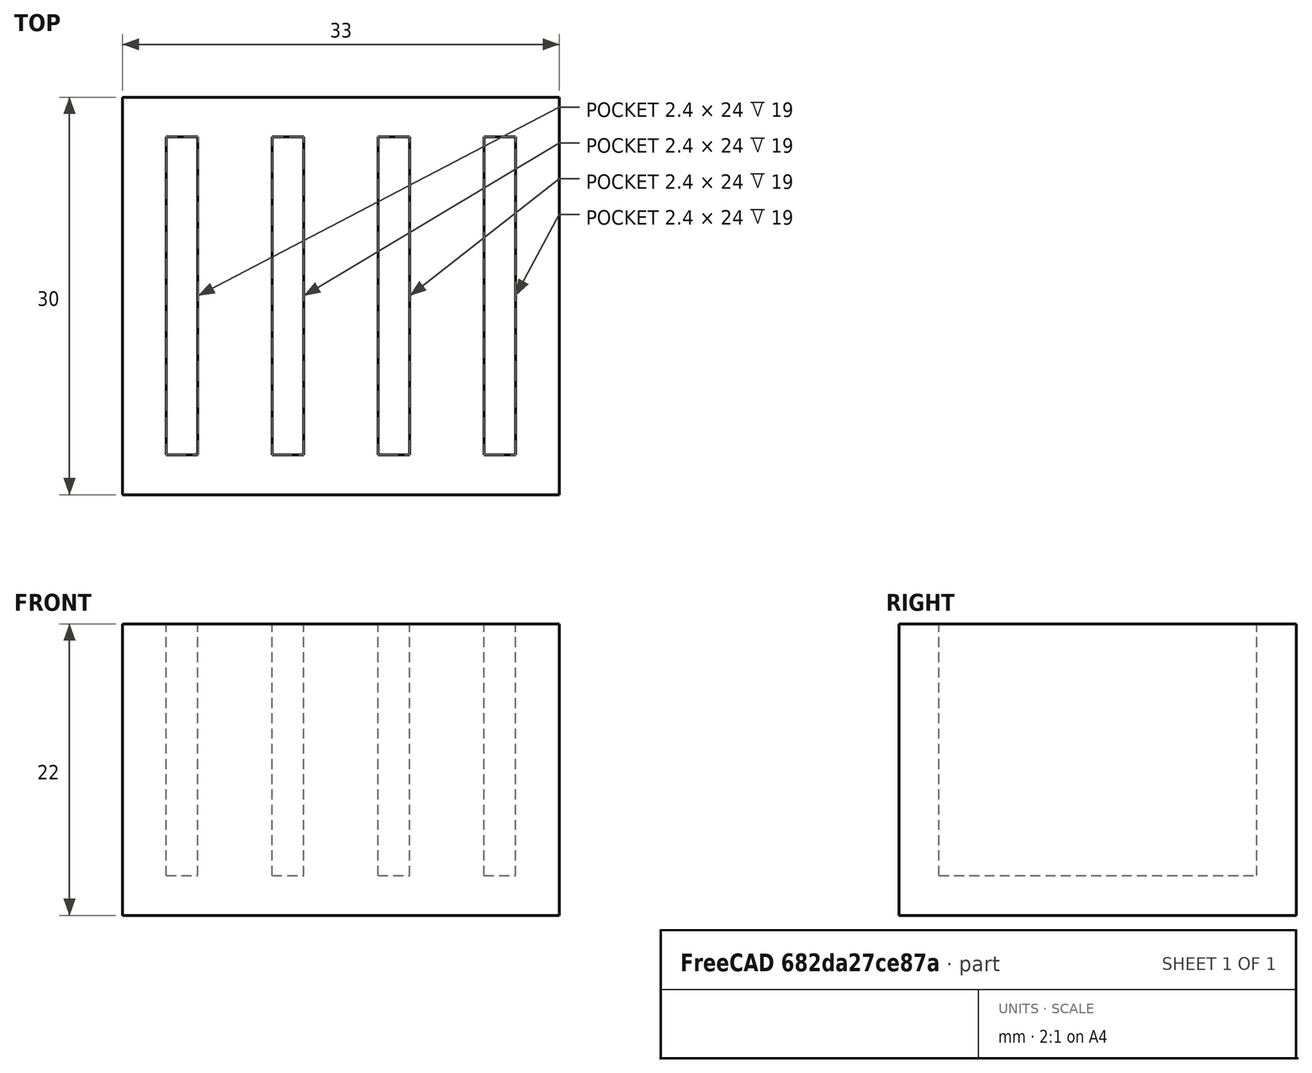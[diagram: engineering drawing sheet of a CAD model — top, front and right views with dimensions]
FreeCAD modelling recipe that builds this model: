
FCSTD DOCUMENT  (FreeCAD 1.0R39319 (Git))
Label: ojt1_t08r01_sd_holder
License: All rights reserved
LicenseURL: https://en.wikipedia.org/wiki/All_rights_reserved
objects: Part::Box×5, PartDesign::Body×1, Part::MultiFuse×1, Part::Cut×1
note: 8 computed .brp shape members not serialized (recipe doc carries the construction recipe); baked Part::Feature solids carry a one-line shape summary decoded from their .brp

FEATURE [PartDesign::Body] Body  label="Cos"
  AllowCompound = false
  Origin = -> Origin
FEATURE [Part::Box] Box004  label="base"
  AttacherType = Attacher::AttachEngine3D
  Height = 22
  Length = 33
  Width = 30
FEATURE [Part::Box] Box  label="cub 1"
  AttacherType = Attacher::AttachEngine3D
  Height = 30
  Length = 2.4
  Placement = pos=(3.3,3,0) rot=(0,0,1;0rad)
  Width = 24
FEATURE [Part::Box] Box007  label="cub 2"
  AttacherType = Attacher::AttachEngine3D
  Height = 30
  Length = 2.4
  Placement = pos=(11.3,3,0) rot=(0,0,1;0rad)
  Width = 24
FEATURE [Part::Box] Box008  label="cub 3"
  AttacherType = Attacher::AttachEngine3D
  Height = 30
  Length = 2.4
  Placement = pos=(19.3,3,0) rot=(0,0,1;0rad)
  Width = 24
FEATURE [Part::Box] Box009  label="cub 4"
  AttacherType = Attacher::AttachEngine3D
  Height = 30
  Length = 2.4
  Placement = pos=(27.3,3,0) rot=(0,0,1;0rad)
  Width = 24
FEATURE [Part::MultiFuse] Fusion
  Placement = pos=(0,0,3) rot=(0,0,1;0rad)
  Shapes = -> [Box,Box007,Box008,Box009]
FEATURE [Part::Cut] Cut
  Base = -> Box004
  Tool = -> Fusion
